# Revit family: IS_Ceraplus_A5505_BIM_DE
name_source: partatom
category: Plumbing Fixtures
revit_build: Autodesk Revit MEP 2015 (Build: 20140606_1530(x64)
units: mm (PartAtom-declared; Revit-internal decimal feet)

## types (1)
- A5505AA - CERAPLUS thermostatic build-in bath shower mixer
    Assembly Code = C1030202
    BIMobject category = Showers
    BOSUseNativeGeometries = 1
    Brand url = http://www.idealstandard.co.uk
    Description = A5505AA CERAPLUS thermostatic build-in bath shower mixer
    EAN code = https://4015413310000
    Edition number = 1
    FaucetFunction = thermostatic
    FaucetOperation = leverhandle
    FaucetType = pillar
    FlushRate = 0 m³
    FlushingRate = 0
    IFC Classification = Valve
    IfcExportAs = IfcValveType
    IfcExportType = BRASSWARE BATH
    Installation instructions = http://www.idealspec.co.uk
    Manufacturer name = Ideal Standard
    ManufacturerURL = www.idealstandard.com
    Material = Brass
    Material main = Brassware
    Model = A5505AA
    ModelNumber = A5505AA
    NBS Reference Code = 35-06-82
    NBS Reference Description = Shower Mixers
    Name = CERAPLUS thermostatic build-in bath shower mixer
    NettWeight = 2,376 kg
    Nominal height = 157
    Nominal width = 157
    NominalDepth = 0 mm  [stored 0 ft]
    NominalHeight = 157 mm  [stored 0.515092 ft]
    NominalLength = 0 mm  [stored 0 ft]
    NominalWidth = 157 mm  [stored 0.515092 ft]
    OmniClass Code = 23.45.55.18
    OmniClass Description = Mixing Faucets
    Product Guid = 16e5b04d-9471-47be-9575-757a101c358d
    Product SKU = A5505
    Product data url = https://bimobject.com
    Product family = Sanitary
    Product group = Shower thermostatic valves
    Product name = Ceraplus Bath & Shower/Thermostat Mixer Bin Kit2
    Product url = www.idealstandard.de/produkte
    ProductInformation = www.idealstandard.de/produkte
    QR code = http://bimobject.com
    Shape = Sculptured
    Space = Internal
    SpareParts = www.idealstandard.de/ersatzteile
    Technical description = www.idealstandard.de/produkte
    URL = www.idealstandard.com
    Uniclass 2.0 Code = PR-35-06-82
    Uniclass 2.0 Description = Shower Mixers
    Uniclass 2015 Code = SL_35_80_80
    Uniclass 2015 Name = Showers
    ValveOperation = lever
    Version = 1
    VolumeUnits = Litres
    WarrantyDurationParts = 5
    WarrantyDurationUnit = year
    Weight Net (Kg) = 2.376
    WorkingPressure = 1-5 Bar

note: [stored X ft] marks values corroborated as IEEE doubles in the binary element streams (Revit-internal decimal feet)

## geometry (parser evidence)
native form markers: Blend x4, Sweep x1
no freeform markers — native parametric forms only
